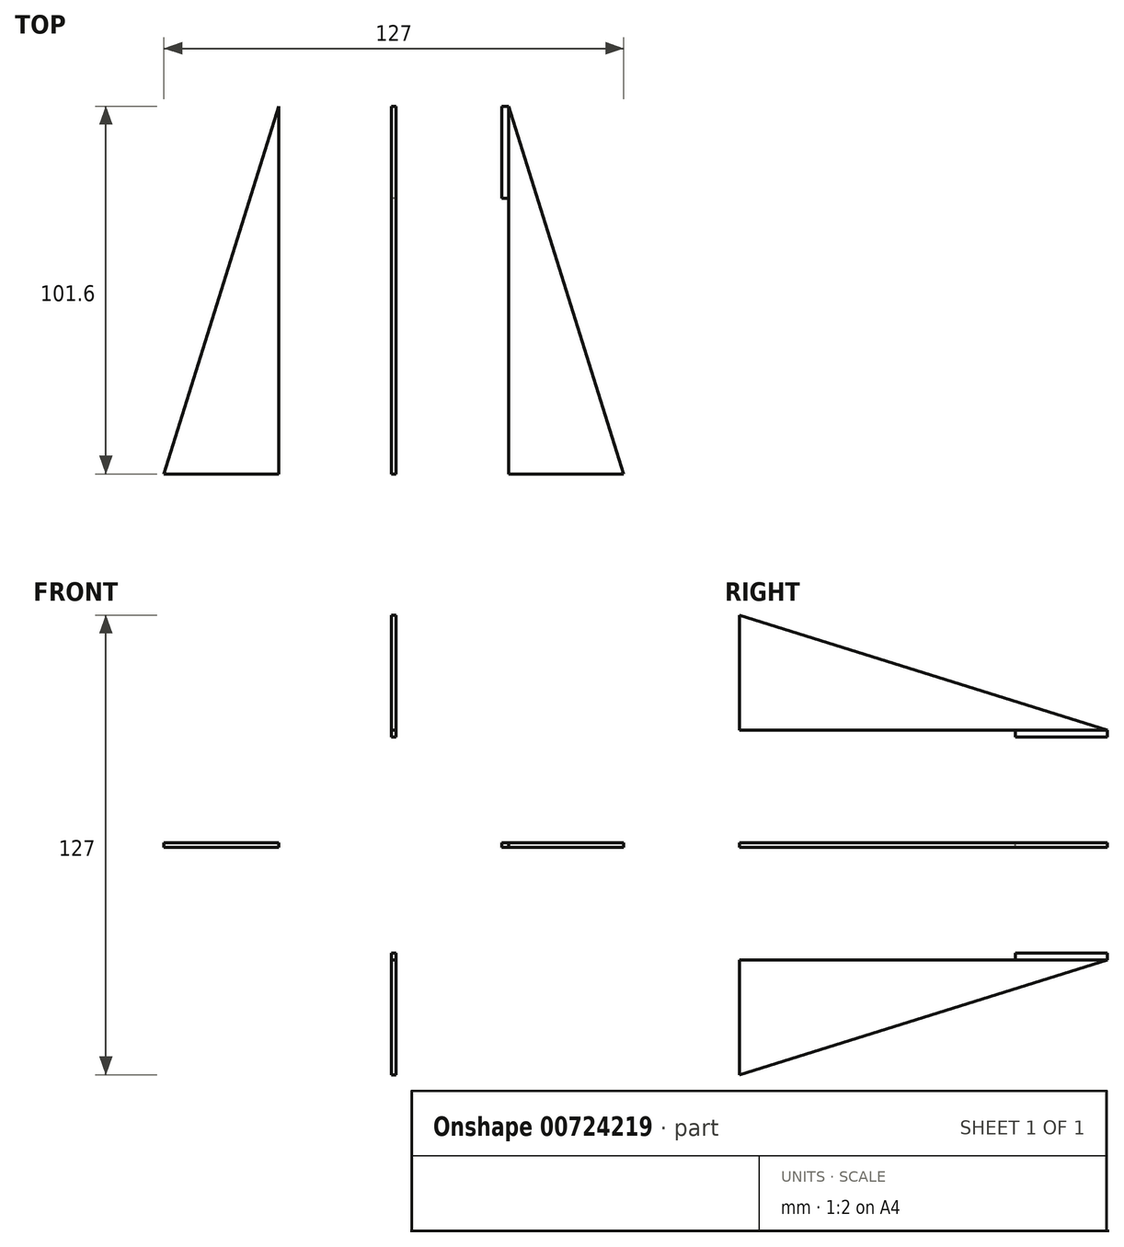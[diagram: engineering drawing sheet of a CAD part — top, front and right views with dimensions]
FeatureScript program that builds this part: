
annotation { "Feature Type Name" : "Feature", "Feature Type Description" : "" }
export const myFeature = defineFeature(function(context is Context, id is Id, definition is map)
    precondition{}
    {
        {
            var Q0;
            Q0=qCreatedBy(makeId("Front.planeOp"),FACE);
            var sketch = newSketch(context, id + "F0", { "sketchPlane" : qUnion([Q0])});
            skCircle(sketch, "E0", {"center": v(0, 0) * mm, "radius": 31.75 * mm});
            skCircle(sketch, "E1", {"center": v(0, 0) * mm, "radius": 29.85 * mm});
            skLineSegment(sketch, "E2.bottom", {"start": v(-0.63, 63.5) * mm, "end": v(0.64, 63.5) * mm});
            skLineSegment(sketch, "E2.top", {"start": v(-0.64, -63.5) * mm, "end": v(0.63, -63.5) * mm});
            skLineSegment(sketch, "E2.left", {"start": v(-0.63, 63.5) * mm, "end": v(-0.64, -63.5) * mm});
            skLineSegment(sketch, "E2.right", {"start": v(0.64, 63.5) * mm, "end": v(0.63, -63.5) * mm});
            skLineSegment(sketch, "E3.bottom", {"start": v(-63.5, 0.63) * mm, "end": v(63.5, 0.63) * mm});
            skLineSegment(sketch, "E3.top", {"start": v(-63.5, -0.64) * mm, "end": v(63.5, -0.64) * mm});
            skLineSegment(sketch, "E3.left", {"start": v(-63.5, 0.63) * mm, "end": v(-63.5, -0.64) * mm});
            skLineSegment(sketch, "E3.right", {"start": v(63.5, 0.63) * mm, "end": v(63.5, -0.64) * mm});
            skSolve(sketch);
        }
        {
            var Q0;
            {var subQ0=sQuery(id+"F0.wireOp",EDGE,"E2.right");var subQ1=sQuery(id+"F0.wireOp",EDGE,"E0");var subQ2=makeQuery(id+"F0.imprint","INTERSECT",VERTEX,{"disambiguationData":[OD(0.0)],"derivedFrom":[subQ1,subQ0]});Q0=makeQuery(id+"F0.imprint","IMPRINT",FACE,{"disambiguationData":[TD([[makeQuery(id+"F0.imprint","IMPRINT",EDGE,{"disambiguationData":[TD([[subQ2,1.0]])],"derivedFrom":subQ1}),1.0]])]});}
            var Q1;
            {var subQ0=sQuery(id+"F0.wireOp",EDGE,"E2.left");var subQ1=sQuery(id+"F0.wireOp",EDGE,"E0");var subQ2=makeQuery(id+"F0.imprint","INTERSECT",VERTEX,{"disambiguationData":[OD(0.0)],"derivedFrom":[subQ1,subQ0]});Q1=makeQuery(id+"F0.imprint","IMPRINT",FACE,{"disambiguationData":[TD([[makeQuery(id+"F0.imprint","IMPRINT",EDGE,{"disambiguationData":[TD([[subQ2,-1.0]])],"derivedFrom":subQ1}),1.0]])]});}
            var Q2;
            {var subQ0=sQuery(id+"F0.wireOp",EDGE,"E3.top");var subQ1=sQuery(id+"F0.wireOp",EDGE,"E0");var subQ2=makeQuery(id+"F0.imprint","INTERSECT",VERTEX,{"disambiguationData":[OD(0.0)],"derivedFrom":[subQ1,subQ0]});Q2=makeQuery(id+"F0.imprint","IMPRINT",FACE,{"disambiguationData":[TD([[makeQuery(id+"F0.imprint","IMPRINT",EDGE,{"disambiguationData":[TD([[subQ2,-1.0]])],"derivedFrom":subQ1}),1.0]])]});}
            var Q3;
            {var subQ0=sQuery(id+"F0.wireOp",EDGE,"E2.right");var subQ1=sQuery(id+"F0.wireOp",EDGE,"E0");var subQ2=makeQuery(id+"F0.imprint","INTERSECT",VERTEX,{"disambiguationData":[OD(1.0)],"derivedFrom":[subQ1,subQ0]});Q3=makeQuery(id+"F0.imprint","IMPRINT",FACE,{"disambiguationData":[TD([[makeQuery(id+"F0.imprint","IMPRINT",EDGE,{"disambiguationData":[TD([[subQ2,-1.0]])],"derivedFrom":subQ1}),1.0]])]});}
            extrude(context, id + "F1", {"entities" : qUnion([Q0, Q1, Q2, Q3]), "depth" : 25.4 * mm, "offsetDistance" : 25.4 * mm});
        }
        {
            var Q0;
            {var subQ5=sQuery(id+"F0.wireOp",EDGE,"E3.left");Q0=makeQuery(id+"F0.imprint","IMPRINT",FACE,{"disambiguationData":[TD([[makeQuery(id+"F0.imprint","IMPRINT",EDGE,{"derivedFrom":subQ5}),1.0]])]});}
            var Q1;
            {var subQ5=sQuery(id+"F0.wireOp",EDGE,"E2.bottom");Q1=makeQuery(id+"F0.imprint","IMPRINT",FACE,{"disambiguationData":[TD([[makeQuery(id+"F0.imprint","IMPRINT",EDGE,{"derivedFrom":subQ5}),-1.0]])]});}
            var Q2;
            {var subQ5=sQuery(id+"F0.wireOp",EDGE,"E3.right");Q2=makeQuery(id+"F0.imprint","IMPRINT",FACE,{"disambiguationData":[TD([[makeQuery(id+"F0.imprint","IMPRINT",EDGE,{"derivedFrom":subQ5}),-1.0]])]});}
            var Q3;
            {var subQ5=sQuery(id+"F0.wireOp",EDGE,"E2.top");Q3=makeQuery(id+"F0.imprint","IMPRINT",FACE,{"disambiguationData":[TD([[makeQuery(id+"F0.imprint","IMPRINT",EDGE,{"derivedFrom":subQ5}),1.0]])]});}
            extrude(context, id + "F2", {"entities" : qUnion([Q0, Q1, Q2, Q3]), "depth" : 101.6 * mm, "offsetDistance" : 25.4 * mm});
        }
        {
            var Q0;
            {var subQ0=sQuery(id+"F0.wireOp",EDGE,"E2.right");Q0=makeQuery(id+"F2.opExtrude","SWEPT_FACE",FACE,{"disambiguationData":[OSD([subQ0]),TDD([makeQuery(id+"F0.imprint","IMPRINT",EDGE,{"disambiguationData":[TD([[makeQuery(id+"F0.imprint","INTERSECT",VERTEX,{"derivedFrom":[sQuery(id+"F0.wireOp",EDGE,"E2.bottom"),subQ0]}),-1.0]])],"derivedFrom":subQ0})])]});}
            var sketch = newSketch(context, id + "F3", { "sketchPlane" : qUnion([Q0])});
            skLineSegment(sketch, "E4", {"start": v(0, 31.74) * mm, "end": v(-101.6, 63.5) * mm});
            skSolve(sketch);
        }
        {
            var Q0;
            Q0=makeQuery(id+"F3.imprint","IMPRINT",FACE,{"disambiguationData":[TD([[makeQuery(id+"F3.imprint","IMPRINT",EDGE,{"derivedFrom":sQuery(id+"F3.wireOp",EDGE,"E4")}),-1.0]])]});
            extrude(context, id + "F4", {"entities" : qUnion([Q0]), "operationType" : NewBodyOperationType.REMOVE, "oppositeDirection" : true, "depth" : 25.4 * mm, "offsetDistance" : 25.4 * mm});
        }
        {
            var Q0;
            {var subQ0=sQuery(id+"F0.wireOp",EDGE,"E3.top");Q0=makeQuery(id+"F2.opExtrude","SWEPT_FACE",FACE,{"disambiguationData":[OSD([subQ0]),TDD([makeQuery(id+"F0.imprint","IMPRINT",EDGE,{"disambiguationData":[TD([[makeQuery(id+"F0.imprint","INTERSECT",VERTEX,{"derivedFrom":[subQ0,sQuery(id+"F0.wireOp",EDGE,"E3.right")]}),1.0]])],"derivedFrom":subQ0})])]});}
            var sketch = newSketch(context, id + "F5", { "sketchPlane" : qUnion([Q0])});
            skLineSegment(sketch, "E5", {"start": v(31.74, 0) * mm, "end": v(63.5, 101.6) * mm});
            skSolve(sketch);
        }
        {
            var Q0;
            Q0=makeQuery(id+"F5.imprint","IMPRINT",FACE,{"disambiguationData":[TD([[makeQuery(id+"F5.imprint","IMPRINT",EDGE,{"derivedFrom":sQuery(id+"F5.wireOp",EDGE,"E5")}),-1.0]])]});
            extrude(context, id + "F6", {"entities" : qUnion([Q0]), "operationType" : NewBodyOperationType.REMOVE, "oppositeDirection" : true, "depth" : 25.4 * mm, "offsetDistance" : 25.4 * mm});
        }
        {
            var Q0;
            {var subQ0=sQuery(id+"F0.wireOp",EDGE,"E3.bottom");Q0=makeQuery(id+"F2.opExtrude","SWEPT_FACE",FACE,{"disambiguationData":[OSD([subQ0]),TDD([makeQuery(id+"F0.imprint","IMPRINT",EDGE,{"disambiguationData":[TD([[makeQuery(id+"F0.imprint","INTERSECT",VERTEX,{"derivedFrom":[subQ0,sQuery(id+"F0.wireOp",EDGE,"E3.left")]}),-1.0]])],"derivedFrom":subQ0})])]});}
            var sketch = newSketch(context, id + "F7", { "sketchPlane" : qUnion([Q0])});
            skLineSegment(sketch, "E6", {"start": v(-31.74, 0) * mm, "end": v(-63.5, -101.6) * mm});
            skSolve(sketch);
        }
        {
            var Q0;
            Q0=makeQuery(id+"F7.imprint","IMPRINT",FACE,{"disambiguationData":[TD([[makeQuery(id+"F7.imprint","IMPRINT",EDGE,{"derivedFrom":sQuery(id+"F7.wireOp",EDGE,"E6")}),-1.0]])]});
            extrude(context, id + "F8", {"entities" : qUnion([Q0]), "operationType" : NewBodyOperationType.REMOVE, "oppositeDirection" : true, "depth" : 25.4 * mm, "offsetDistance" : 25.4 * mm});
        }
        {
            var Q0;
            {var subQ0=sQuery(id+"F0.wireOp",EDGE,"E2.right");Q0=makeQuery(id+"F2.opExtrude","SWEPT_FACE",FACE,{"disambiguationData":[OSD([subQ0]),TDD([makeQuery(id+"F0.imprint","IMPRINT",EDGE,{"disambiguationData":[TD([[makeQuery(id+"F0.imprint","INTERSECT",VERTEX,{"derivedFrom":[sQuery(id+"F0.wireOp",EDGE,"E2.top"),subQ0]}),1.0]])],"derivedFrom":subQ0})])]});}
            var sketch = newSketch(context, id + "F9", { "sketchPlane" : qUnion([Q0])});
            skLineSegment(sketch, "E7", {"start": v(0, -31.74) * mm, "end": v(-101.6, -63.5) * mm});
            skSolve(sketch);
        }
        {
            var Q0;
            Q0=makeQuery(id+"F9.imprint","IMPRINT",FACE,{"disambiguationData":[TD([[makeQuery(id+"F9.imprint","IMPRINT",EDGE,{"derivedFrom":sQuery(id+"F9.wireOp",EDGE,"E7")}),1.0]])]});
            extrude(context, id + "F10", {"entities" : qUnion([Q0]), "operationType" : NewBodyOperationType.REMOVE, "oppositeDirection" : true, "depth" : 25.4 * mm, "offsetDistance" : 25.4 * mm});
        }
    });
